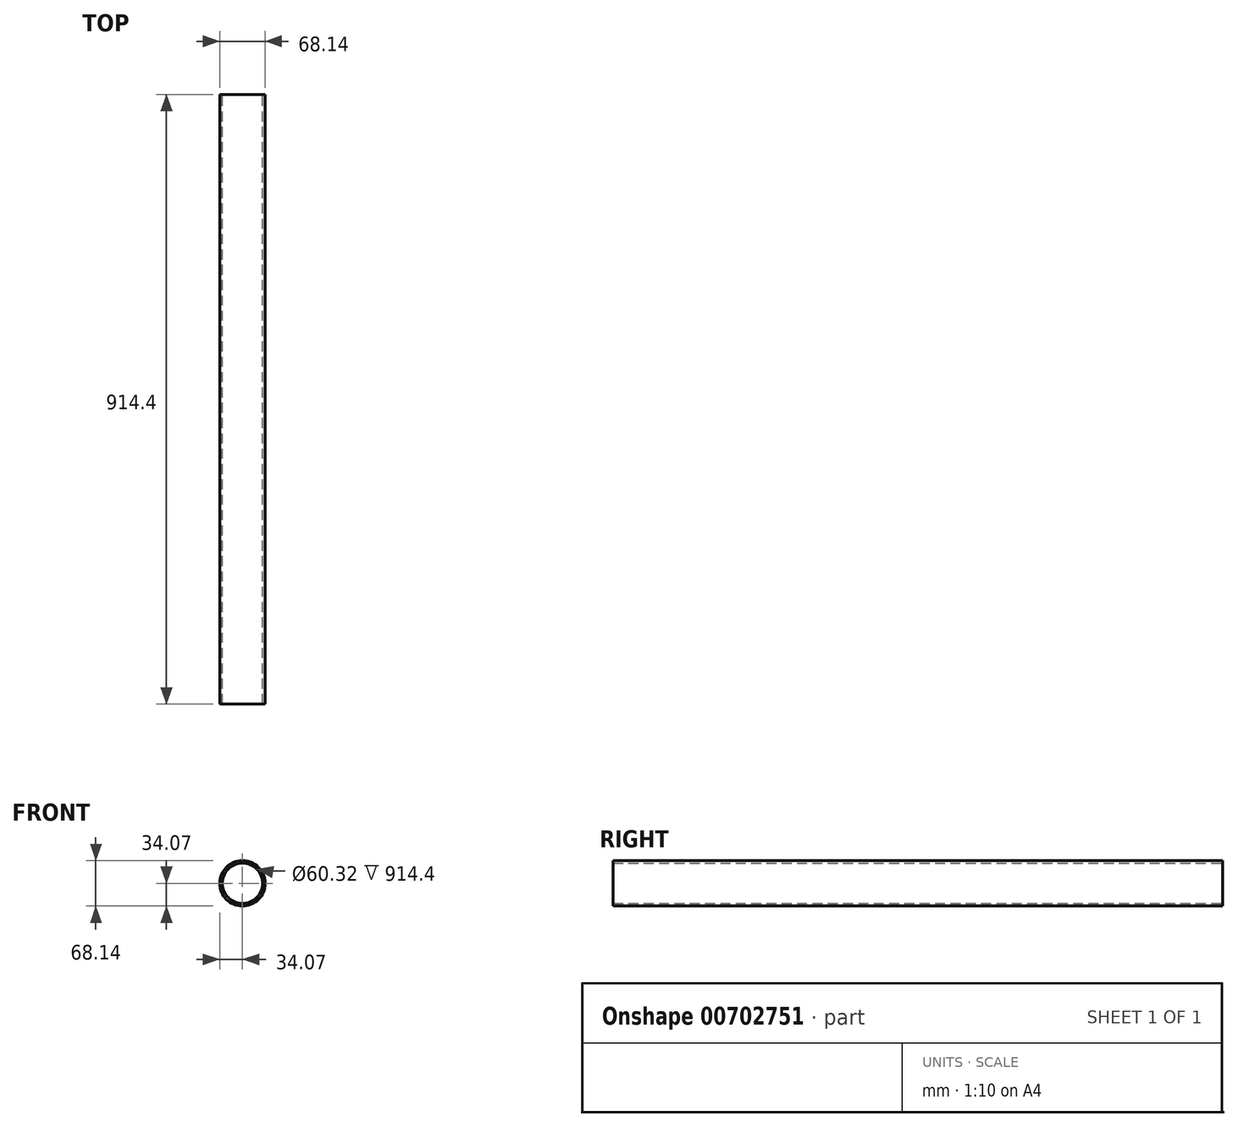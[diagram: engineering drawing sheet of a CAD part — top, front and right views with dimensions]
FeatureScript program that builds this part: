
annotation { "Feature Type Name" : "Feature", "Feature Type Description" : "" }
export const myFeature = defineFeature(function(context is Context, id is Id, definition is map)
    precondition{}
    {
        {
            var Q0;
            Q0=qCreatedBy(makeId("Front.planeOp"),FACE);
            var sketch = newSketch(context, id + "F0", { "sketchPlane" : qUnion([Q0])});
            skCircle(sketch, "E0", {"center": v(0, 0) * mm, "radius": 30.16 * mm});
            skCircle(sketch, "E1", {"center": v(0, 0) * mm, "radius": 34.07 * mm});
            skSolve(sketch);
        }
        {
            var Q0;
            Q0 = qSketchRegion(id + "F0", true);
            extrude(context, id + "F1", {"entities" : qUnion([Q0]), "depth" : 914.4 * mm, "offsetDistance" : 25.4 * mm});
        }
    });
